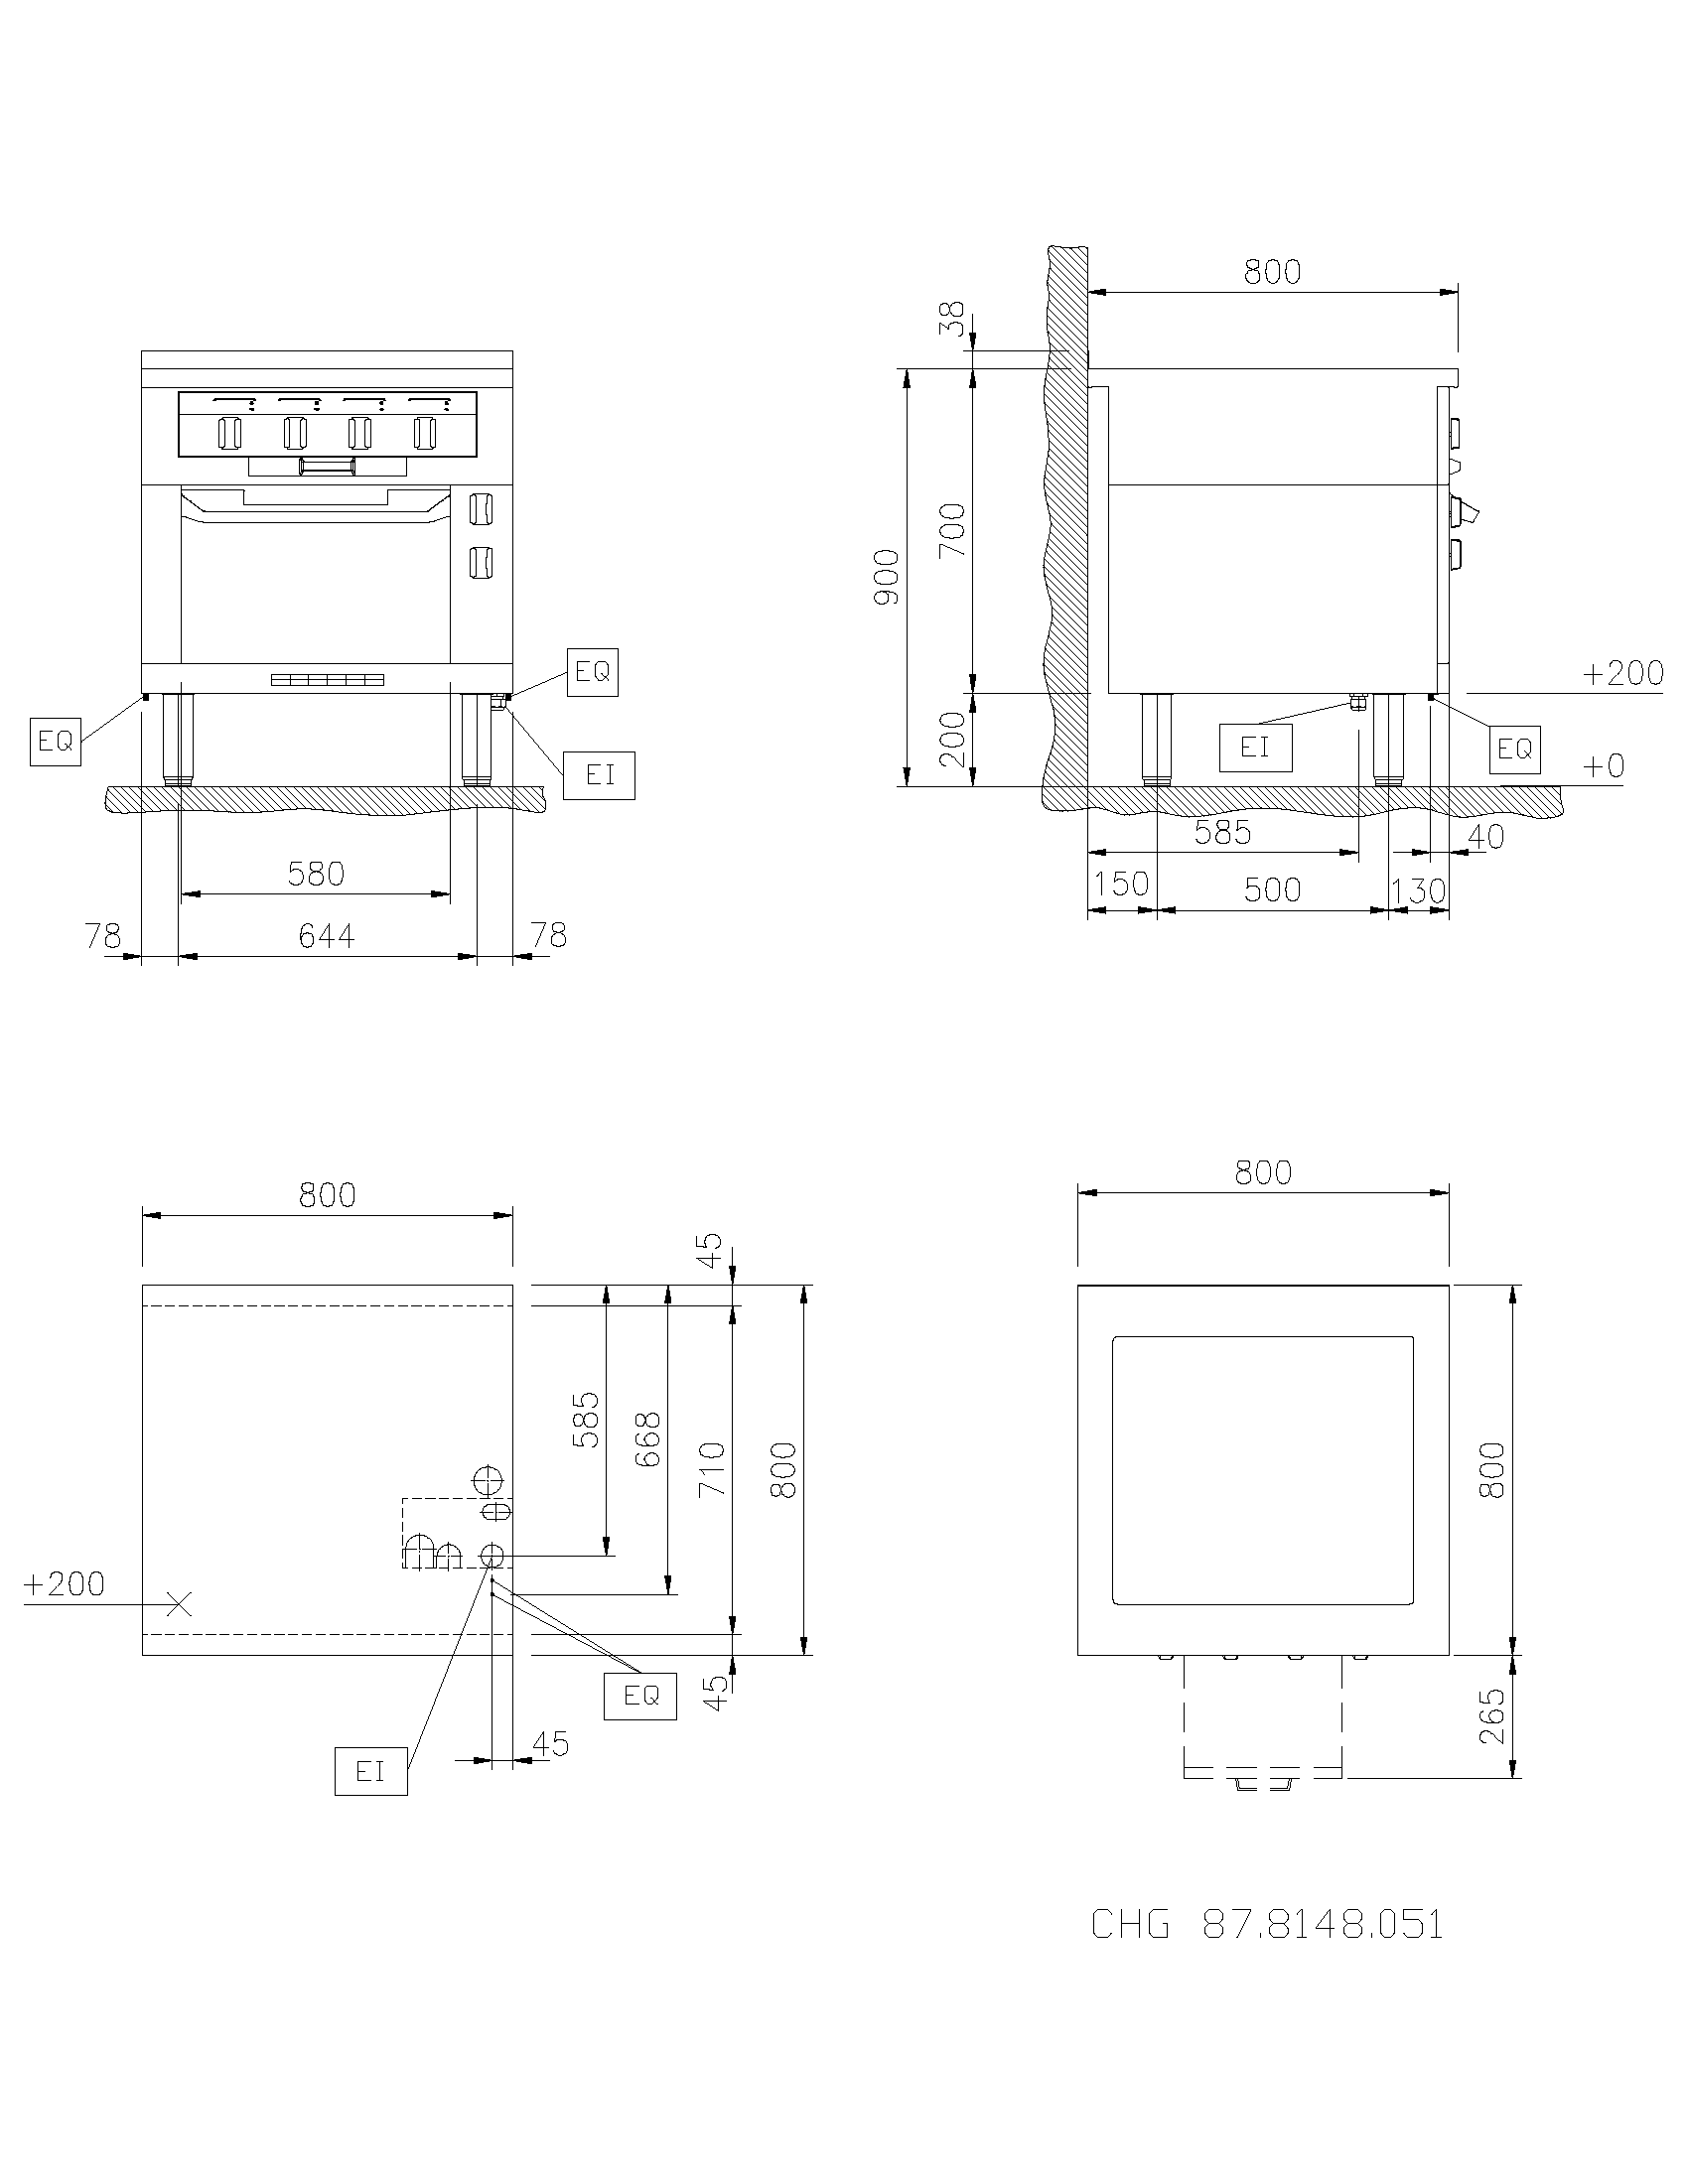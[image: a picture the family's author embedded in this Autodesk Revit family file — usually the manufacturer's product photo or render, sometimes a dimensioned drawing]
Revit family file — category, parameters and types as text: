
# Revit family: QF_ELECTROLUXPROFESSIONAL_588468_MALSFCH4AO
name_source: partatom
category: Attrezzature speciali
units: mm (PartAtom-declared; Revit-internal decimal feet)

## family parameters
Basato su piano di lavoro = No
Condiviso = No
Punto di calcolo locali = No
Quota connettore circolare = Usa diametro
Sempre verticale = Sì
Taglio con vuoti quando caricato = No
Tipo di parte = Normale

## types (1)
- Standard
    Accessory = Sì
    Cold Water Size = 0"
    Compressed Air Pressure = 0.00 psi
    Compressed Air Size = 0"
    Compressed Air Volume = 0 GPM
    Condensate Return Size = 0"
    Cycle = 50 Hz
    Depth Actual = 800 mm  [stored 2.62467 ft]
    Descrizione = EL.SOLID T,ECO,WARM.C,PASS,2S,800X800X8
    Direct Waste Size = 0"
    Gas Input Pressure = 0.0
    Gas KW = 0
    Gas Size = 0"
    HP = 19.2 HP
    Height Actual = 800 mm  [stored 2.62467 ft]
    Hot Water Size = 0"
    Item Number = 588468
    Length Actual = 800 mm  [stored 2.62467 ft]
    Modello = MALSFCH4AO
    Phase = 3
    Produttore = Electrolux Professional
    Prospetto di default = 0 mm  [stored 0 ft]
    Refrigerant Compressor Remote = Sì
    Refrigeration Liquid Line Size = 0 mm  [stored 0 ft]
    Refrigeration Suction Line Size = 0 mm  [stored 0 ft]
    Steam Consumption per Hour = 0
    Steam Supply Maximum Pressure = 0.00 psi
    Steam Supply Minimum Pressure = 0.00 psi
    Steam Supply Size = 0"
    URL = https://www.electroluxprofessional.com
    URL Manufacturer = https://www.electroluxprofessional.com
    Volts = 400 V
    Watts = 14300 W
    Weight = 147.00 kg

note: source unit labels omitted for Gas Input Pressure — the stored unit's dimension contradicts the parameter name (converter mislabeling)

note: [stored X ft] marks values corroborated as IEEE doubles in the binary element streams (Revit-internal decimal feet)

## geometry (parser evidence)
native form markers: Blend x12, Sweep x15
no freeform markers — native parametric forms only
